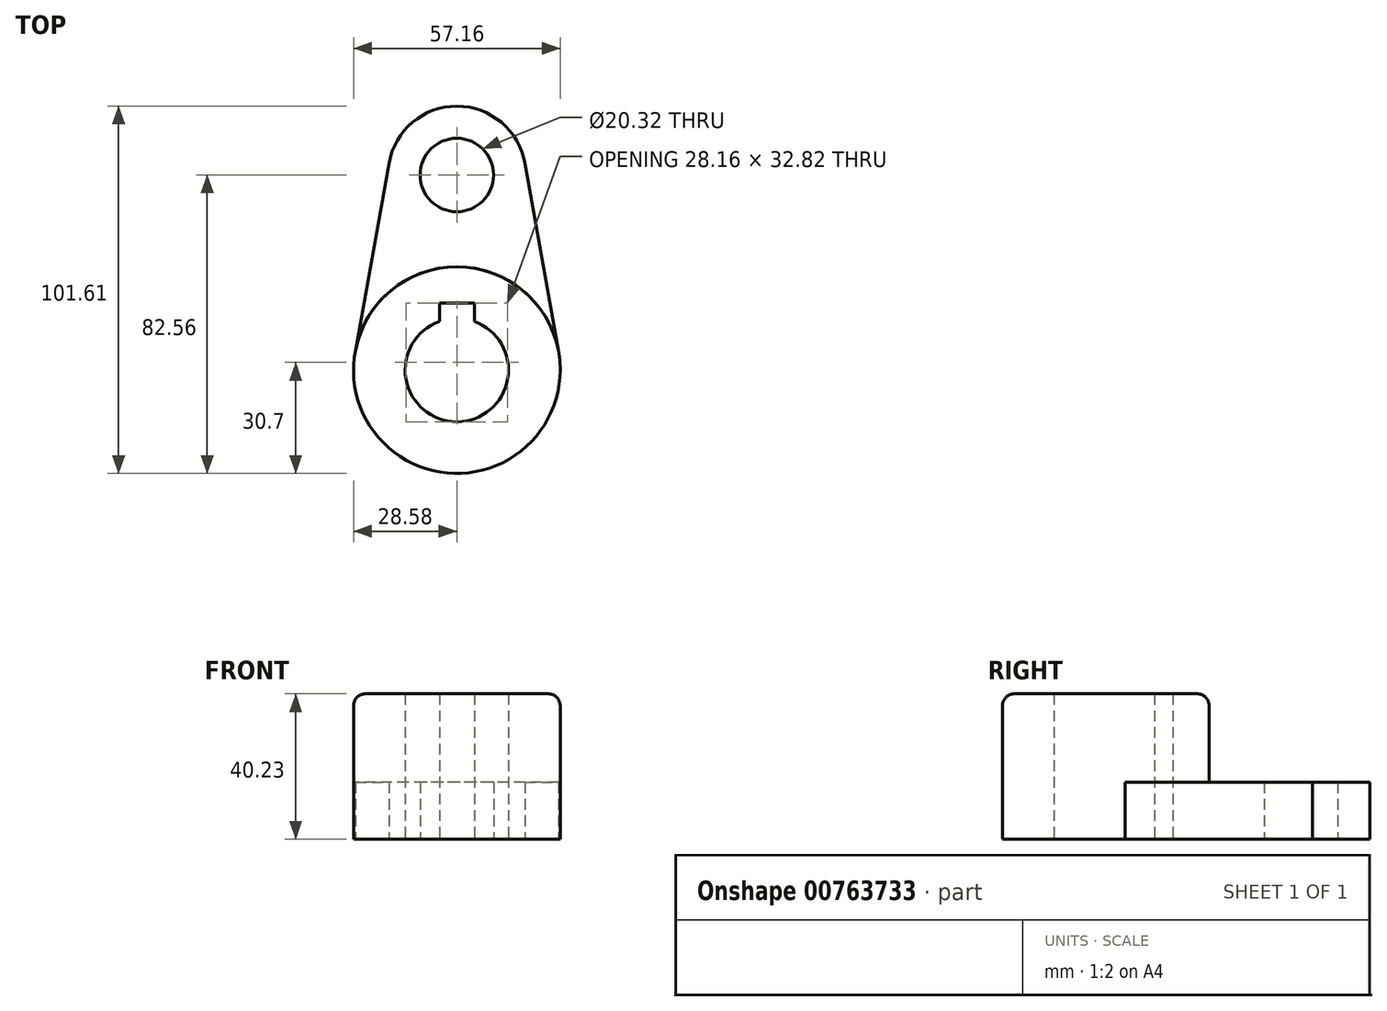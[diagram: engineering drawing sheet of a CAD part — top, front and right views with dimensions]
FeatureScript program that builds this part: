
annotation { "Feature Type Name" : "Feature", "Feature Type Description" : "" }
export const myFeature = defineFeature(function(context is Context, id is Id, definition is map)
    precondition{}
    {
        {
            var Q0;
            Q0=qCreatedBy(makeId("Top.planeOp"),FACE);
            var sketch = newSketch(context, id + "F0", { "sketchPlane" : qUnion([Q0])});
            skCircle(sketch, "E0", {"center": v(0, 0) * mm, "radius": 28.58 * mm});
            skCircle(sketch, "E1", {"center": v(0, 0) * mm, "radius": 14.29 * mm});
            skCircle(sketch, "E2", {"center": v(0, 53.98) * mm, "radius": 10.16 * mm});
            skCircle(sketch, "E3", {"center": v(0, 53.98) * mm, "radius": 19.05 * mm});
            skLineSegment(sketch, "E4", {"start": v(-28.13, 5.04) * mm, "end": v(-18.75, 57.34) * mm});
            skLineSegment(sketch, "E5", {"start": v(18.75, 57.34) * mm, "end": v(28.13, 5.04) * mm});
            skLineSegment(sketch, "E6.bottom", {"start": v(0, 0) * mm, "end": v(4.83, 0) * mm});
            skLineSegment(sketch, "E6.top", {"start": v(0, 18.53) * mm, "end": v(4.83, 18.53) * mm});
            skLineSegment(sketch, "E6.right", {"start": v(4.83, 0) * mm, "end": v(4.83, 18.53) * mm});
            skLineSegment(sketch, "E7.MirrorCS", {"start": v(0, 0) * mm, "end": v(-4.83, 0) * mm});
            skLineSegment(sketch, "E8.MirrorCS", {"start": v(0, 18.53) * mm, "end": v(-4.83, 18.53) * mm});
            skLineSegment(sketch, "E9.MirrorCS", {"start": v(-18.75, 57.34) * mm, "end": v(-28.13, 5.04) * mm});
            skLineSegment(sketch, "E10.MirrorCS", {"start": v(-4.83, 0) * mm, "end": v(-4.83, 18.53) * mm});
            skSolve(sketch);
        }
        {
            var Q0;
            {var subQ4=sQuery(id+"F0.wireOp",EDGE,"E6.top");Q0=makeQuery(id+"F0.imprint","IMPRINT",FACE,{"disambiguationData":[TD([[makeQuery(id+"F0.imprint","IMPRINT",EDGE,{"derivedFrom":subQ4}),1.0]])]});}
            extrude(context, id + "F1", {"entities" : qUnion([Q0]), "depth" : 40.23 * mm, "offsetDistance" : 25.4 * mm});
        }
        {
            var Q0;
            Q0=makeQuery(id+"F1.opExtrude","CAP_EDGE",EDGE,{"disambiguationData":[OSD([sQuery(id+"F0.wireOp",EDGE,"E0")])],"isStart":false});
            fillet(context, id + "F2", {"entities" : qUnion([Q0]), "radius" : 3.3 * mm, "tangentPropagation" : true, "allowEdgeOverflow" : false});
        }
        {
            var Q0;
            {var subQ0=sQuery(id+"F0.wireOp",EDGE,"E5");Q0=makeQuery(id+"F0.imprint","IMPRINT",FACE,{"disambiguationData":[TD([[makeQuery(id+"F0.imprint","IMPRINT",EDGE,{"derivedFrom":subQ0}),-1.0]])]});}
            var Q1;
            Q1=makeQuery(id+"F0.imprint","IMPRINT",FACE,{"disambiguationData":[TD([[makeQuery(id+"F0.imprint","IMPRINT",EDGE,{"derivedFrom":sQuery(id+"F0.wireOp",EDGE,"E2")}),-1.0]])]});
            extrude(context, id + "F3", {"entities" : qUnion([Q0, Q1]), "operationType" : NewBodyOperationType.ADD, "depth" : 15.77 * mm, "offsetDistance" : 25.4 * mm});
        }
    });
